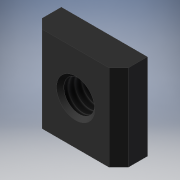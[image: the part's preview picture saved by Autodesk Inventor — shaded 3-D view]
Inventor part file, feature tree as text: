
AUTODESK INVENTOR PART (.ipt)
format: ipt  version: 2025 (Build 290162000, 162)  size: 129,536 bytes
history: native  units: mm
features: sketch x3, extrude x2, revolve x1, thread x1
ambient origin geometry x8: Origin, YZ Plane, XZ Plane, XY Plane, X Axis, Y Axis, Z Axis, Center Point
bodies: Solid1 (feature_tree)
feature tree (7):
  extrude  "Extrusion1"  TaperAngle=360.0deg  [1 undecoded]
  revolve  "Revolution1"  [1 undecoded]
  thread  "Thread1"  [1 undecoded]
  extrude  "Extrusion2"  [1 undecoded]
  sketch  "Sketch_1"  dims[d0=3.0mm d1=0.0mm d2=360.0deg]
  sketch  "Sketch_2"  dims[d3=2.242mm d4=0.0mm d5=18.0mm d6=0.0mm]
  sketch  "Sketch_3"
note: 4 required parameter values undecoded (feature->parameter linkage not recoverable at this tier; creation-order binding heuristic only, values carry confidence <= 0.55)